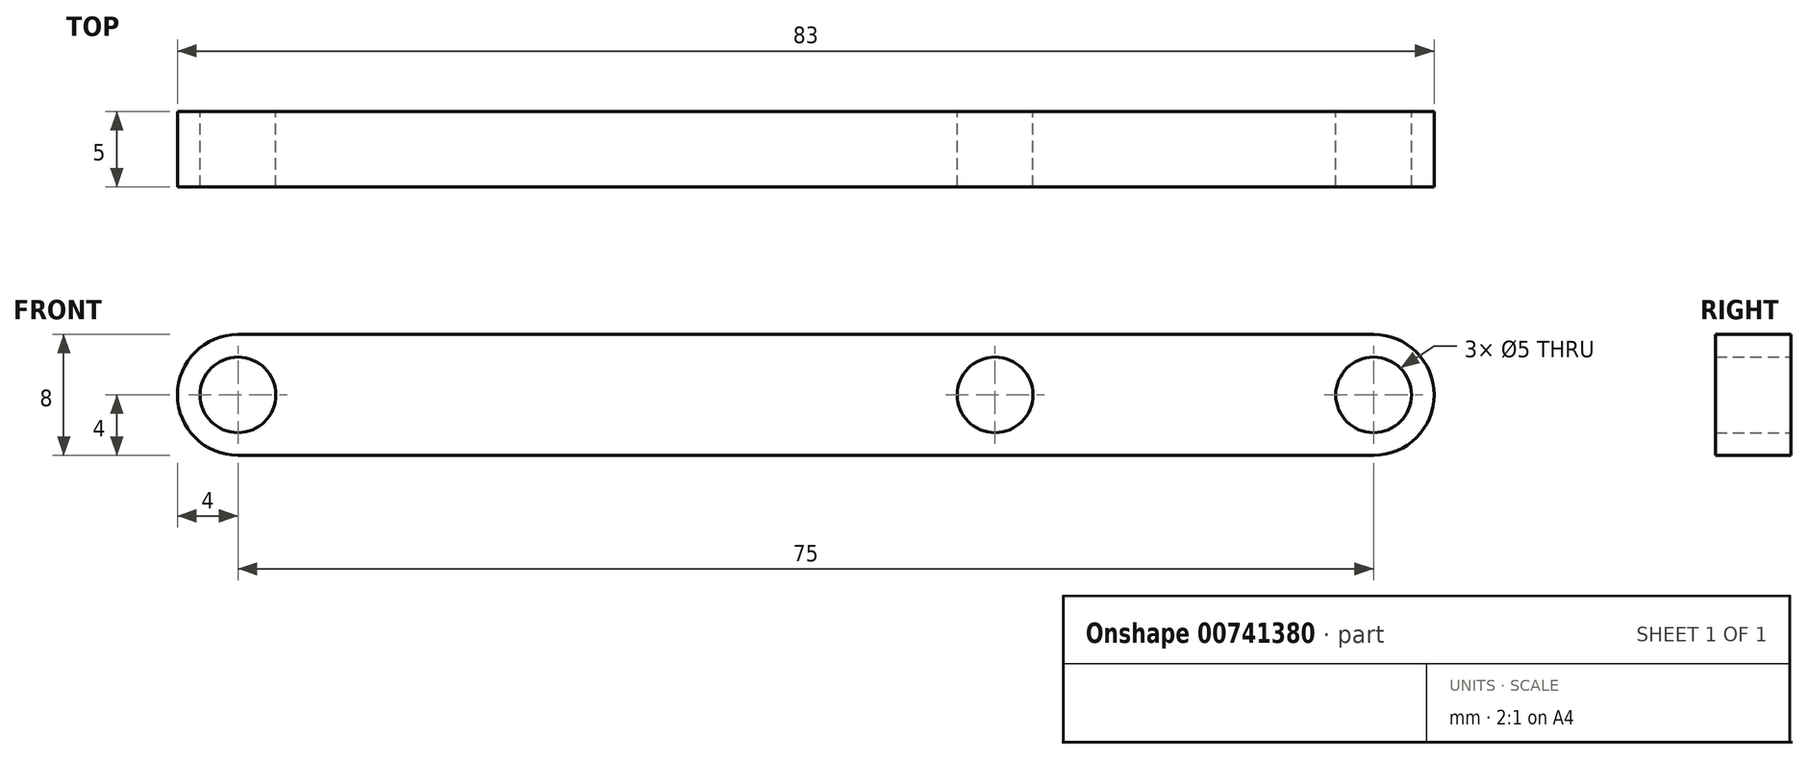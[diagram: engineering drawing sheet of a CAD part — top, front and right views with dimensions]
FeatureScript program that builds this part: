
annotation { "Feature Type Name" : "Feature", "Feature Type Description" : "" }
export const myFeature = defineFeature(function(context is Context, id is Id, definition is map)
    precondition{}
    {
        {
            var Q0;
            Q0=qCreatedBy(makeId("Front.planeOp"),FACE);
            var sketch = newSketch(context, id + "F0", { "sketchPlane" : qUnion([Q0])});
            skArc(sketch, "E0", {"start": v(0, 4) * mm, "mid": v(-4, 0) * mm, "end": v(0, -4) * mm});
            skCircle(sketch, "E1", {"center": v(50, 0) * mm, "radius": 2.5 * mm});
            skArc(sketch, "E2", {"start": v(75, -4) * mm, "mid": v(79, 0) * mm, "end": v(75, 4) * mm});
            skCircle(sketch, "E3", {"center": v(0, 0) * mm, "radius": 2.5 * mm});
            skCircle(sketch, "E4", {"center": v(75, 0) * mm, "radius": 2.5 * mm});
            skLineSegment(sketch, "E5", {"start": v(0, 4) * mm, "end": v(75, 4) * mm});
            skLineSegment(sketch, "E6", {"start": v(0, -4) * mm, "end": v(75, -4) * mm});
            skSolve(sketch);
        }
        {
            var Q0;
            Q0=makeQuery(id+"F0.imprint","IMPRINT",FACE,{"disambiguationData":[TD([[makeQuery(id+"F0.imprint","IMPRINT",EDGE,{"derivedFrom":sQuery(id+"F0.wireOp",EDGE,"E0")}),1.0]])]});
            extrude(context, id + "F1", {"entities" : qUnion([Q0]), "depth" : 5 * mm, "offsetDistance" : 25 * mm});
        }
    });
